# Revit family: ZEPHYR CARRÉ
name_source: partatom
category: Luminaires
units: mm (PartAtom-declared; Revit-internal decimal feet)

## family parameters
Cote de connecteur circulaire = Utiliser le diamètre
Couper avec des vides une fois chargée = Oui
Hôte = Face
Numéro OmniClass = 23.80.70.11.14.11
Partagée = Oui
Point de calcul de pièce = Oui
Source d'éclairage = Oui
Titre OmniClass = Downlights
Type d'élément = Normal

## types (2) — shared parameters
Angle de l'inclinaison = 60.00°
Charge apparente = 20 VA
Commentaires relatifs à la puissance = 18.8W
Coût = 53.75 $
Emettre la visibilité des formes dans le rendu = Non
Emettre à partir de la largeur du rectangle = 610 mm
Emettre à partir de la longueur du rectangle = 1219 mm
Fabricant = Résistex
Fichier de distribution photométrique = 791904.ies
Filtre de couleur = 16777215
Garantie = 5 ans
Gradation des changements de température de couleur de lampe = <Aucun>
IK = 08
IP = 40
Image du type = <Aucun>
Indice de charge = Eclairage
Largeur = 224 mm
Largeur 2 = 240 mm  [stored 0.787402 ft]
Largeur diffuseur = 190 mm
Matériau diffuseur = PC Transparent
Modèle = Zephyr
Nombre pôles = 1
Tension = 230 V
URL = https://www.resistex-sa.com
Épaisseur = 10 mm  [stored 0.0328084 ft]
Épaisseur 2 = 1 mm  [stored 0.00328084 ft]
Épaisseur collerette = 2 mm  [stored 0.00656168 ft]
zero-valued in all types: Elévation par défaut

## per-type parameters (varying)
| type | Description |
| 791904 | Downlight équipé d'un module LED SMD, efficacité lumineuse de 75.4lm/W |
| 791905 | Downlight équipé d'un module LED SMD, efficacité lumineuse de 80.9lm/W |

note: [stored X ft] marks values corroborated as IEEE doubles in the binary element streams (Revit-internal decimal feet)
